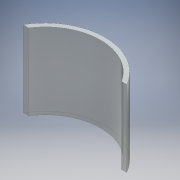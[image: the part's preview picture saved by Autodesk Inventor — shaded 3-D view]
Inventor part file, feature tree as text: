
AUTODESK INVENTOR PART (.ipt)
format: ipt  version: 2016 (Build 200138000, 138)  size: 103,936 bytes
history: native  units: mm
features: extrude x1, sketch x1
ambient origin geometry x8: Origin, YZ Plane, XZ Plane, XY Plane, X Axis, Y Axis, Z Axis, Center Point
bodies: Body1 (feature_tree)
feature tree (2):
  extrude  "押し出し2"  Depth=70.5mm TaperAngle=0.0deg
  sketch  "スケッチ2"
